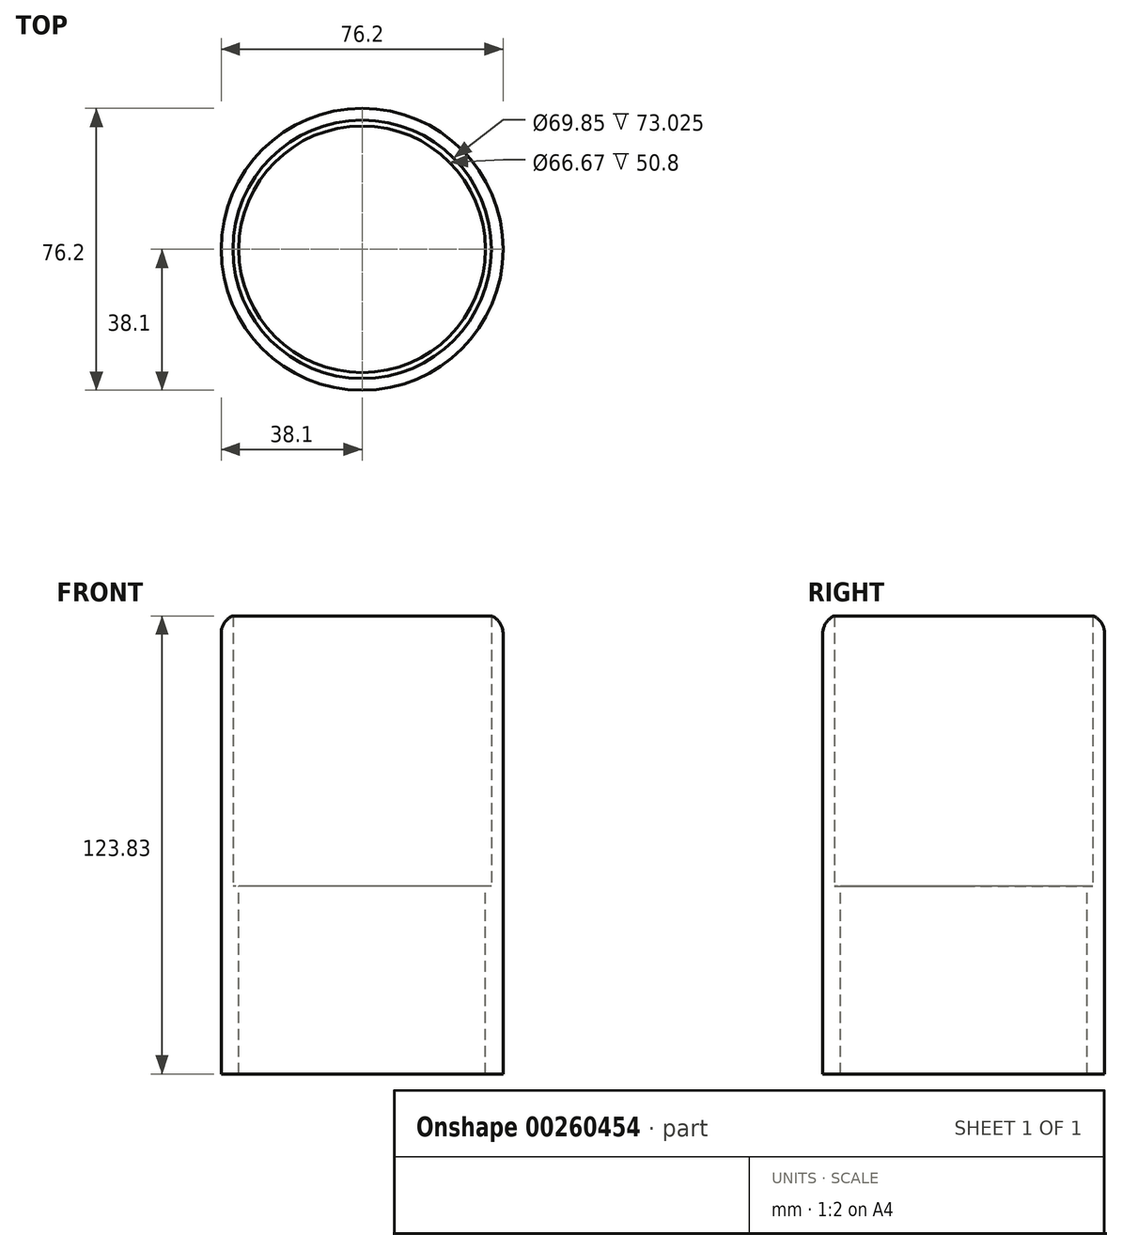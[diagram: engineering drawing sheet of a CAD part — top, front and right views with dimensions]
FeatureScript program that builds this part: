
annotation { "Feature Type Name" : "Feature", "Feature Type Description" : "" }
export const myFeature = defineFeature(function(context is Context, id is Id, definition is map)
    precondition{}
    {
        {
            var Q0;
            Q0=qCreatedBy(makeId("Top.planeOp"),FACE);
            var sketch = newSketch(context, id + "F0", { "sketchPlane" : qUnion([Q0])});
            skCircle(sketch, "E0", {"center": v(0, 0) * mm, "radius": 34.93 * mm});
            skCircle(sketch, "E1", {"center": v(0, 0) * mm, "radius": 38.1 * mm});
            skSolve(sketch);
        }
        {
            var Q0;
            Q0 = qSketchRegion(id + "F0", true);
            extrude(context, id + "F1", {"entities" : qUnion([Q0]), "depth" : 73.02 * mm});
        }
        {
            var Q0;
            Q0=qCreatedBy(makeId("Top.planeOp"),FACE);
            var sketch = newSketch(context, id + "F2", { "sketchPlane" : qUnion([Q0])});
            skCircle(sketch, "E2", {"center": v(0, 0) * mm, "radius": 38.1 * mm});
            skCircle(sketch, "E3", {"center": v(0, 0) * mm, "radius": 33.34 * mm});
            skSolve(sketch);
        }
        {
            var Q0;
            Q0=makeQuery(id+"F2.imprint","IMPRINT",FACE,{"disambiguationData":[TD([[makeQuery(id+"F2.imprint","IMPRINT",EDGE,{"derivedFrom":sQuery(id+"F2.wireOp",EDGE,"E2")}),1.0]])]});
            extrude(context, id + "F3", {"entities" : qUnion([Q0]), "operationType" : NewBodyOperationType.ADD, "oppositeDirection" : true, "depth" : 50.8 * mm});
        }
        {
            var Q0;
            Q0=makeQuery(id+"F1.opExtrude","CAP_EDGE",EDGE,{"disambiguationData":[OSD([sQuery(id+"F0.wireOp",EDGE,"E1")])],"isStart":false});
            fillet(context, id + "F4", {"entities" : qUnion([Q0]), "radius" : 5.08 * mm, "tangentPropagation" : true, "allowEdgeOverflow" : false});
        }
    });
